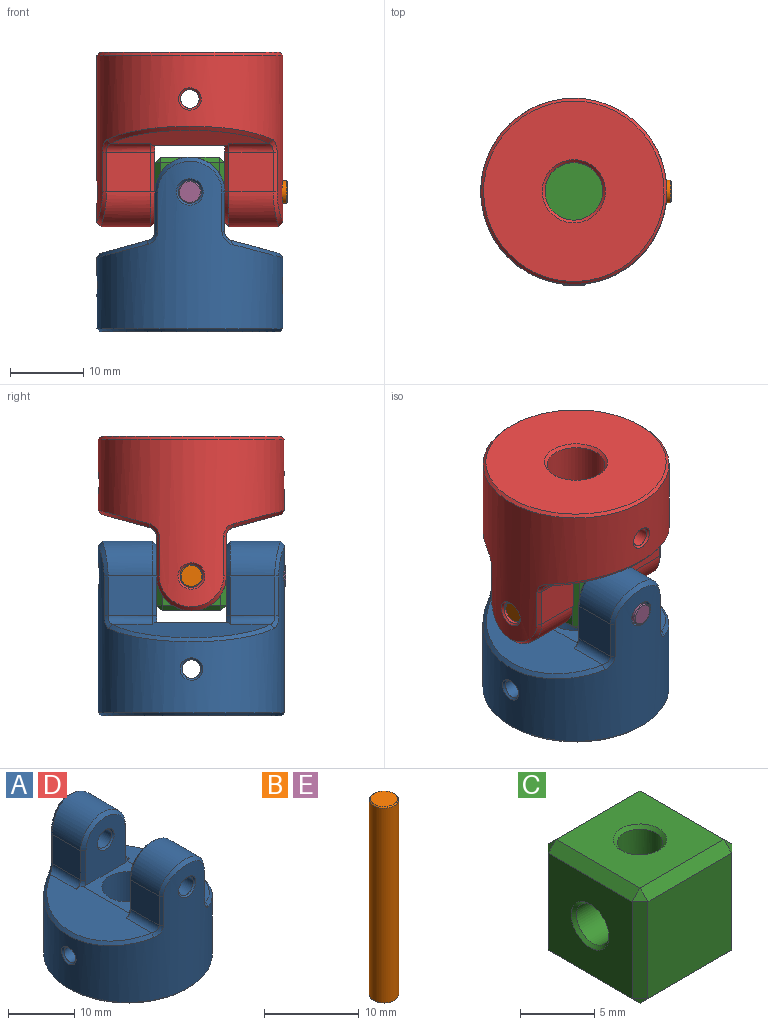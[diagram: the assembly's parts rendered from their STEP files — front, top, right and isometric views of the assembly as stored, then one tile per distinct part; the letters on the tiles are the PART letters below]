
ASSEMBLY  parts=5 mates=5
PART A: 52 faces, bbox 25.6x25.6x24.1 mm
  f0: cylinder r=12.7mm len=25.4mm, axis (0,0,1), area 1016.8mm2, adj f16,f19,f20,f21,f22,f30,f31,f32
  f1: plane 10.03x9.54mm, normal (0,0,1), area 42.2mm2, adj f2,f3,f6,f24,f25,f42,f46,f47
  f2: cylinder r=3.94mm len=12.32mm, axis (0,0,1), area 294.5mm2, adj f1,f14,f15,f23
  f3: plane 10.54x8.93mm, normal (0,-1,0), area 70.7mm2, adj f1,f18,f42,f43,f44,f45,f46
  f4: plane 6.05x5.38mm, normal (1,0,0), area 32.5mm2, adj f12,f28,f34,f43
  f5: plane 6.05x5.38mm, normal (-1,0,0), area 32.5mm2, adj f12,f26,f38,f45
  f6: plane 10.54x8.93mm, normal (0,1,0), area 70.7mm2, adj f1,f17,f47,f48,f49,f50,f51
  f7: plane 24.64x24.64mm, normal (0,0,-1), area 418.2mm2, adj f16,f23
  f8: plane 6.05x5.38mm, normal (1,0,0), area 32.5mm2, adj f10,f27,f33,f48
  f9: plane 6.05x5.38mm, normal (-1,0,0), area 32.5mm2, adj f10,f29,f37,f50
  f10: cylinder r=4.76mm len=9.53mm, axis (0,1,0), area 90.5mm2, adj f8,f9,f35,f49
  f11: cylinder r=1.55mm len=7.43mm, axis (0,1,0), area 72.3mm2, adj f17,f19
  f12: cylinder r=4.76mm len=9.53mm, axis (0,-1,0), area 90.5mm2, adj f4,f5,f36,f44
  f13: cylinder r=1.55mm len=7.43mm, axis (0,-1,0), area 72.3mm2, adj f18,f20
  f14: cylinder r=1.27mm len=8.51mm, axis (-1,0,0), area 67.9mm2, adj f2,f21
  f15: cylinder r=1.27mm len=8.51mm, axis (1,0,0), area 67.9mm2, adj f2,f22
  f16: cone r=12.7mm half-angle=45deg, axis (0,0,1), area 42.4mm2, adj f0,f7
  f17: cone r=1.8mm half-angle=45deg, axis (0,1,0), area 3.8mm2, adj f6,f11
  f18: cone r=1.8mm half-angle=45deg, axis (0,-1,0), area 3.8mm2, adj f3,f13
  f19: bspline ~3.68x3.61mm, area 3.9mm2, adj f0,f11
  f20: bspline ~3.68x3.61mm, area 3.9mm2, adj f0,f13
  f21: bspline ~3.11x3.05mm, area 3.3mm2, adj f0,f14
  f22: bspline ~3.11x3.05mm, area 3.3mm2, adj f0,f15
  f23: cone r=4.32mm half-angle=45deg, axis (0,0,-1), area 14mm2, adj f2,f7
  f24: plane 21.81x7.76mm, normal (-0.27,0,0.96), area 115.3mm2, adj f1,f26,f29,f41,f46,f51
  f25: plane 21.81x7.76mm, normal (0.27,0,0.96), area 115.3mm2, adj f1,f27,f28,f30,f42,f47
  f26: cylinder r=1.27mm len=6.05mm, axis (0,-1,0), area 9.5mm2, adj f5,f24,f40,f46
  f27: cylinder r=1.27mm len=6.05mm, axis (0,-1,0), area 9.5mm2, adj f8,f25,f31,f47
  f28: cylinder r=1.27mm len=6.05mm, axis (0,-1,0), area 9.5mm2, adj f4,f25,f32,f42
  f29: cylinder r=1.27mm len=6.05mm, axis (0,-1,0), area 9.5mm2, adj f9,f24,f39,f51
  f30: bspline ~22.59x7.01mm, area 19.7mm2, adj f0,f25,f31,f32
  f31: bspline ~1.78x1.43mm, area 1.5mm2, adj f0,f27,f30,f33
  f32: bspline ~1.78x1.43mm, area 1.5mm2, adj f0,f28,f30,f34
  f33: plane 5.38x0.54mm, normal (0.82,-0.57,0), area 3.5mm2, adj f0,f8,f31,f35
  f34: plane 5.38x0.54mm, normal (0.82,0.57,0), area 3.5mm2, adj f0,f4,f32,f36
  f35: bspline ~9.53x4.76mm, area 10.5mm2, adj f0,f10,f33,f37
  f36: bspline ~9.53x4.76mm, area 10.5mm2, adj f0,f12,f34,f38
  f37: plane 5.38x0.54mm, normal (-0.82,-0.57,0), area 3.5mm2, adj f0,f9,f35,f39
  f38: plane 5.38x0.54mm, normal (-0.82,0.57,0), area 3.5mm2, adj f0,f5,f36,f40
  f39: bspline ~1.78x1.43mm, area 1.5mm2, adj f0,f29,f37,f41
  f40: bspline ~1.78x1.43mm, area 1.5mm2, adj f0,f26,f38,f41
  f41: bspline ~22.59x7.01mm, area 19.7mm2, adj f0,f24,f39,f40
  f42: cone r=1.84mm half-angle=45deg, axis (0,-1,0), area 1mm2, adj f1,f3,f25,f28,f43
  f43: plane 5.38x0.57mm, normal (0.71,-0.71,0), area 4.4mm2, adj f3,f4,f42,f44
  f44: cone r=4.76mm half-angle=45deg, axis (0,1,0), area 11.4mm2, adj f3,f12,f43,f45
  f45: plane 5.38x0.57mm, normal (-0.71,-0.71,0), area 4.4mm2, adj f3,f5,f44,f46
  f46: cone r=1.84mm half-angle=45deg, axis (0,-1,0), area 1mm2, adj f1,f3,f24,f26,f45
  f47: cone r=1.84mm half-angle=45deg, axis (0,1,0), area 1mm2, adj f1,f6,f25,f27,f48
  f48: plane 5.38x0.57mm, normal (0.71,0.71,0), area 4.4mm2, adj f6,f8,f47,f49
  f49: cone r=4.76mm half-angle=45deg, axis (0,-1,0), area 11.4mm2, adj f6,f10,f48,f50
  f50: plane 5.38x0.57mm, normal (-0.71,0.71,0), area 4.4mm2, adj f6,f9,f49,f51
  f51: cone r=1.84mm half-angle=45deg, axis (0,1,0), area 1mm2, adj f1,f6,f24,f29,f50
PART B: 5 faces, bbox 3.1x3.1x25.4 mm
  f0: cylinder r=1.55mm len=25.15mm, axis (0,0,-1), area 244.8mm2, adj f3,f4
  f1: plane 2.85x2.85mm, normal (0,0,1), area 6.4mm2, adj f4
  f2: plane 2.85x2.85mm, normal (0,0,-1), area 6.4mm2, adj f3
  f3: cone r=1.55mm half-angle=45deg, axis (0,0,1), area 1.7mm2, adj f0,f2
  f4: cone r=1.42mm half-angle=45deg, axis (0,0,-1), area 1.7mm2, adj f0,f1
PART C: 38 faces, bbox 9.5x9.5x9.5 mm
  f0: cylinder r=1.55mm len=4.51mm, axis (0,0,-1), area 33.5mm2, adj f1,f36,f37
  f1: bspline ~3.1x1.68mm, area 0mm2, adj f0,f2
  f2: cylinder r=1.55mm len=4.51mm, axis (1,0,0), area 34.6mm2, adj f1,f3,f35
  f3: bspline ~3.1x1.68mm, area 0.1mm2, adj f2,f4
  f4: cylinder r=1.55mm len=4.51mm, axis (0,0,-1), area 33.5mm2, adj f3,f5,f34
  f5: bspline ~3.1x1.68mm, area 0.3mm2, adj f4,f6
  f6: cylinder r=1.55mm len=4.51mm, axis (1,0,0), area 34.6mm2, adj f5,f7,f36
  f7: cone r=1.8mm half-angle=45deg, axis (-1,0,0), area 3.8mm2, adj f6,f8
  f8: plane 8x8mm, normal (-1,0,0), area 53.8mm2, adj f7,f9,f31,f32,f33
  f9: plane 8x0.76mm, normal (-0.71,0.71,0), area 8.6mm2, adj f8,f10,f29,f30
  f10: plane 0.76x0.76mm, normal (-0.58,0.58,-0.58), area 0.5mm2, adj f9,f11,f33
  f11: plane 8x0.76mm, normal (0,0.71,-0.71), area 8.6mm2, adj f10,f12,f28,f29
  f12: plane 8x8mm, normal (0,0,-1), area 53.8mm2, adj f11,f13,f27,f33,f34
  f13: plane 8x0.76mm, normal (0,-0.71,-0.71), area 8.6mm2, adj f12,f14,f15,f26
  f14: plane 0.76x0.76mm, normal (-0.58,-0.58,-0.58), area 0.5mm2, adj f13,f32,f33
  f15: plane 8x8mm, normal (0,-1,0), area 64mm2, adj f13,f16,f25,f32
  f16: plane 8x0.76mm, normal (0,-0.71,0.71), area 8.6mm2, adj f15,f17,f18,f24
  f17: plane 0.76x0.76mm, normal (-0.58,-0.58,0.58), area 0.5mm2, adj f16,f31,f32
  f18: plane 8x8mm, normal (0,0,1), area 53.8mm2, adj f16,f19,f23,f31,f37
  f19: plane 8x0.76mm, normal (0,0.71,0.71), area 8.6mm2, adj f18,f20,f29,f30
  f20: plane 0.76x0.76mm, normal (0.58,0.58,0.58), area 0.5mm2, adj f19,f21,f23
  f21: plane 8x0.76mm, normal (0.71,0.71,0), area 8.6mm2, adj f20,f22,f28,f29
  f22: plane 8x8mm, normal (1,0,0), area 53.8mm2, adj f21,f23,f25,f27,f35
  f23: plane 8x0.76mm, normal (0.71,0,0.71), area 8.6mm2, adj f18,f20,f22,f24
  f24: plane 0.76x0.76mm, normal (0.58,-0.58,0.58), area 0.5mm2, adj f16,f23,f25
  f25: plane 8x0.76mm, normal (0.71,-0.71,0), area 8.6mm2, adj f15,f22,f24,f26
  f26: plane 0.76x0.76mm, normal (0.58,-0.58,-0.58), area 0.5mm2, adj f13,f25,f27
  f27: plane 8x0.76mm, normal (0.71,0,-0.71), area 8.6mm2, adj f12,f22,f26,f28
  f28: plane 0.76x0.76mm, normal (0.58,0.58,-0.58), area 0.5mm2, adj f11,f21,f27
  f29: plane 8x8mm, normal (0,1,0), area 64mm2, adj f9,f11,f19,f21
  f30: plane 0.76x0.76mm, normal (-0.58,0.58,0.58), area 0.5mm2, adj f9,f19,f31
  f31: plane 8x0.76mm, normal (-0.71,0,0.71), area 8.6mm2, adj f8,f17,f18,f30
  f32: plane 8x0.76mm, normal (-0.71,-0.71,0), area 8.6mm2, adj f8,f14,f15,f17
  f33: plane 8x0.76mm, normal (-0.71,0,-0.71), area 8.6mm2, adj f8,f10,f12,f14
  f34: cone r=1.8mm half-angle=45deg, axis (0,0,-1), area 3.8mm2, adj f4,f12
  f35: cone r=1.55mm half-angle=45deg, axis (1,0,0), area 3.8mm2, adj f2,f22
  f36: bspline ~3.1x1.68mm, area 0mm2, adj f0,f6
  f37: cone r=1.55mm half-angle=45deg, axis (0,0,1), area 3.8mm2, adj f0,f18
PART D: same geometry as A
PART E: same geometry as B
PLACE A t=(60.82,11.01,2.61)mm
PLACE B rot(axis=(0,-1,0),90deg) t=(61.42,11.01,8.96)mm
PLACE C rot(axis=(0,0.71,0.71),180deg) t=(60.82,11.01,8.96)mm
PLACE D rot(axis=(-0.71,-0.71,0),180deg) t=(60.82,11.01,15.31)mm
PLACE E rot(axis=(-0.58,-0.58,-0.58),120deg) t=(60.82,10.85,8.96)mm
MATE cylindrical E.f0 <-> A.f11  axis (0,-1,0) through (60.82,-1.72,8.96)mm
MATE cylindrical C.f0 <-> E.f0  axis (0,1,0) through (60.82,15.52,8.96)mm
MATE cylindrical B.f0 <-> D.f11  axis (1,0,0) through (74.12,11.01,8.96)mm
MATE planar C.f2 <-> D.f11  axis (-1,0,0) through (56.06,11.01,8.96)mm
MATE cylindrical B.f0 <-> C.f2  axis (1,0,0) through (48.84,11.01,8.96)mm
